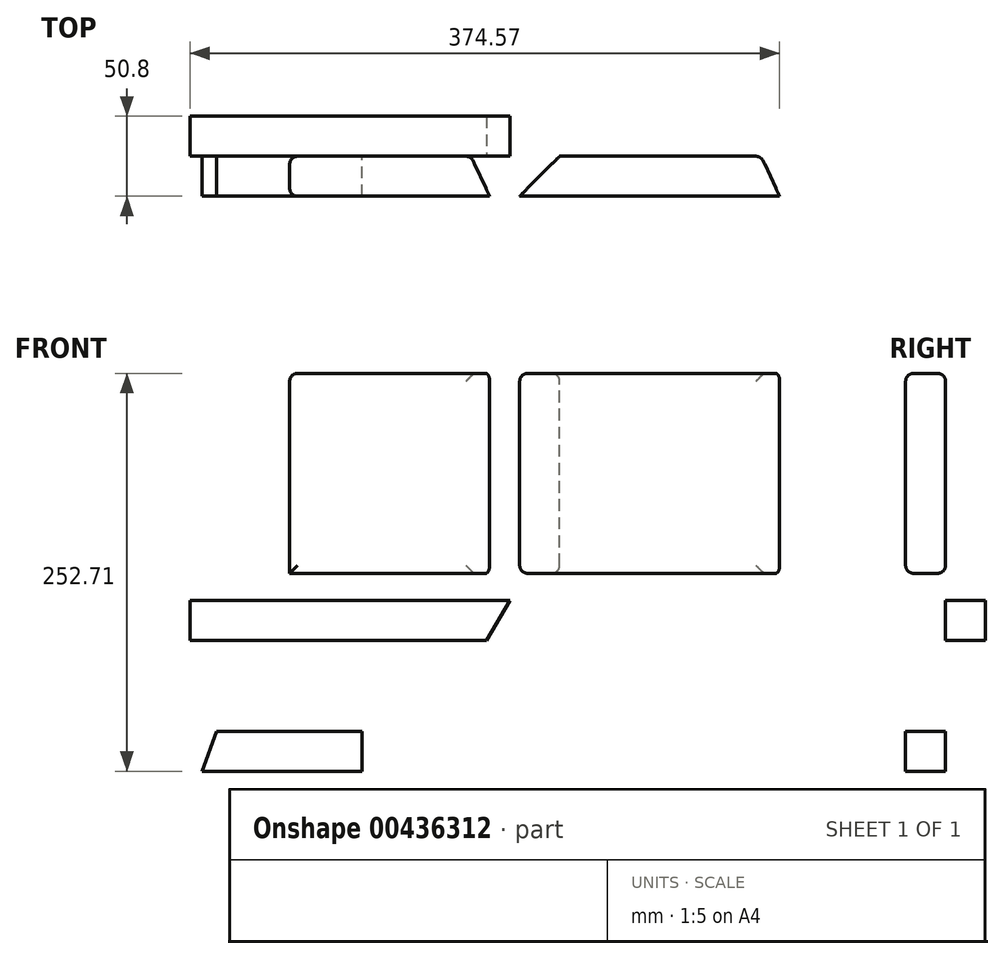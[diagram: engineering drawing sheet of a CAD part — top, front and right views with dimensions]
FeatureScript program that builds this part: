
annotation { "Feature Type Name" : "Feature", "Feature Type Description" : "" }
export const myFeature = defineFeature(function(context is Context, id is Id, definition is map)
    precondition{}
    {
        {
            var Q0;
            Q0=qCreatedBy(makeId("Front.planeOp"),FACE);
            var sketch = newSketch(context, id + "F0", { "sketchPlane" : qUnion([Q0])});
            skLineSegment(sketch, "E0", {"start": v(0, 0) * mm, "end": v(127, 0) * mm});
            skLineSegment(sketch, "E1", {"start": v(127, 0) * mm, "end": v(127, 127) * mm});
            skLineSegment(sketch, "E2", {"start": v(127, 127) * mm, "end": v(0, 127) * mm});
            skLineSegment(sketch, "E3", {"start": v(0, 127) * mm, "end": v(0, 0) * mm});
            skSolve(sketch);
        }
        {
            var Q0;
            Q0 = qSketchRegion(id + "F0", true);
            extrude(context, id + "F1", {"entities" : qUnion([Q0]), "depth" : 25.4 * mm});
        }
        {
            var Q0;
            Q0=makeQuery(id+"F1.opExtrude","CAP_EDGE",EDGE,{"disambiguationData":[OSD([sQuery(id+"F0.wireOp",EDGE,"E1")])],"isStart":true});
            chamfer(context, id + "F2", {"entities" : qUnion([Q0]), "chamferType" : ChamferType.OFFSET_ANGLE, "width" : 25.4 * mm, "oppositeDirection" : false, "angle" : 25 * degree, "tangentPropagation" : true});
        }
        {
            var Q0;
            Q0=qCreatedBy(makeId("Front.planeOp"),FACE);
            var sketch = newSketch(context, id + "F3", { "sketchPlane" : qUnion([Q0])});
            skLineSegment(sketch, "E4.bottom", {"start": v(146.1, 127) * mm, "end": v(311.2, 127) * mm});
            skLineSegment(sketch, "E4.top", {"start": v(146.1, 0) * mm, "end": v(311.2, 0) * mm});
            skLineSegment(sketch, "E4.left", {"start": v(146.1, 127) * mm, "end": v(146.1, 0) * mm});
            skLineSegment(sketch, "E4.right", {"start": v(311.2, 127) * mm, "end": v(311.2, 0) * mm});
            skSolve(sketch);
        }
        {
            var Q0;
            Q0 = qSketchRegion(id + "F3", true);
            extrude(context, id + "F4", {"entities" : qUnion([Q0]), "depth" : 25.4 * mm});
        }
        {
            var Q0;
            Q0=makeQuery(id+"F4.opExtrude","CAP_EDGE",EDGE,{"disambiguationData":[OSD([sQuery(id+"F3.wireOp",EDGE,"E4.right")])],"isStart":true});
            chamfer(context, id + "F5", {"entities" : qUnion([Q0]), "chamferType" : ChamferType.OFFSET_ANGLE, "width" : 25.4 * mm, "oppositeDirection" : true, "angle" : 25 * degree});
        }
        {
            var Q0;
            Q0=makeQuery(id+"F4.opExtrude","CAP_EDGE",EDGE,{"disambiguationData":[OSD([sQuery(id+"F3.wireOp",EDGE,"E4.left")])],"isStart":true});
            chamfer(context, id + "F6", {"entities" : qUnion([Q0]), "chamferType" : ChamferType.OFFSET_ANGLE, "width" : 25.4 * mm, "oppositeDirection" : false, "angle" : 45 * degree, "tangentPropagation" : true});
        }
        {
            var Q0;
            Q0=makeQuery(id+"F1.opExtrude","CAP_FACE",FACE,{"disambiguationData":[OSD([sQuery(id+"F0.wireOp",EDGE,"E0"),sQuery(id+"F0.wireOp",EDGE,"E1"),sQuery(id+"F0.wireOp",EDGE,"E2"),sQuery(id+"F0.wireOp",EDGE,"E3")])],"isStart":true});
            var sketch = newSketch(context, id + "F7", { "sketchPlane" : qUnion([Q0])});
            skLineSegment(sketch, "E5.bottom", {"start": v(63.38, -17.34) * mm, "end": v(-139.82, -17.34) * mm});
            skLineSegment(sketch, "E5.top", {"start": v(63.38, -42.74) * mm, "end": v(-139.82, -42.74) * mm});
            skLineSegment(sketch, "E5.left", {"start": v(63.38, -17.34) * mm, "end": v(63.38, -42.74) * mm});
            skLineSegment(sketch, "E5.right", {"start": v(-139.82, -17.34) * mm, "end": v(-139.82, -42.74) * mm});
            skSolve(sketch);
        }
        {
            var Q0;
            Q0 = qSketchRegion(id + "F7", true);
            extrude(context, id + "F8", {"entities" : qUnion([Q0]), "depth" : 25.4 * mm});
        }
        {
            var Q0;
            Q0=makeQuery(id+"F8.opExtrude","SWEPT_EDGE",EDGE,{"disambiguationData":[OSD([sQuery(id+"F7.wireOp",EDGE,"E5.top"),sQuery(id+"F7.wireOp",EDGE,"E5.right")])]});
            chamfer(context, id + "F9", {"entities" : qUnion([Q0]), "chamferType" : ChamferType.OFFSET_ANGLE, "width" : 25.4 * mm, "oppositeDirection" : true, "angle" : 30 * degree, "tangentPropagation" : true});
        }
        {
            var Q0;
            Q0=makeQuery(id+"F1.opExtrude","CAP_EDGE",EDGE,{"disambiguationData":[OSD([sQuery(id+"F0.wireOp",EDGE,"E2")])],"isStart":false});
            var Q1;
            Q1=makeQuery(id+"F1.opExtrude","CAP_EDGE",EDGE,{"disambiguationData":[OSD([sQuery(id+"F0.wireOp",EDGE,"E2")])],"isStart":true});
            var Q2;
            Q2=makeQuery(id+"F1.opExtrude","CAP_EDGE",EDGE,{"disambiguationData":[OSD([sQuery(id+"F0.wireOp",EDGE,"E3")])],"isStart":false});
            var Q3;
            Q3=makeQuery(id+"F1.opExtrude","SWEPT_EDGE",EDGE,{"disambiguationData":[OSD([sQuery(id+"F0.wireOp",EDGE,"E2"),sQuery(id+"F0.wireOp",EDGE,"E3")])]});
            var Q4;
            Q4=makeQuery(id+"F1.opExtrude","CAP_EDGE",EDGE,{"disambiguationData":[OSD([sQuery(id+"F0.wireOp",EDGE,"E0")])],"isStart":false});
            var Q5;
            Q5=makeQuery(id+"F4.opExtrude","CAP_EDGE",EDGE,{"disambiguationData":[OSD([sQuery(id+"F3.wireOp",EDGE,"E4.top")])],"isStart":true});
            var Q6;
            {var subQ0=sQuery(id+"F3.wireOp",EDGE,"E4.right");Q6=makeQuery(id+"F5.opChamfer","BLEND_EDGE",EDGE,{"blendedFrom":[makeQuery(id+"F4.opExtrude","CAP_EDGE",EDGE,{"disambiguationData":[OSD([subQ0])],"isStart":true}),makeQuery(id+"F4.opExtrude","CAP_FACE",FACE,{"disambiguationData":[OSD([sQuery(id+"F3.wireOp",EDGE,"E4.bottom"),sQuery(id+"F3.wireOp",EDGE,"E4.top"),sQuery(id+"F3.wireOp",EDGE,"E4.left"),subQ0])],"isStart":true})],"blendedInto":[makeQuery(id+"F4.opExtrude","CAP_FACE",FACE,{"disambiguationData":[OSD([sQuery(id+"F3.wireOp",EDGE,"E4.bottom"),sQuery(id+"F3.wireOp",EDGE,"E4.top"),sQuery(id+"F3.wireOp",EDGE,"E4.left"),subQ0])],"isStart":true})]});}
            var Q7;
            Q7=makeQuery(id+"F4.opExtrude","CAP_EDGE",EDGE,{"disambiguationData":[OSD([sQuery(id+"F3.wireOp",EDGE,"E4.bottom")])],"isStart":true});
            var Q8;
            Q8=makeQuery(id+"F4.opExtrude","CAP_EDGE",EDGE,{"disambiguationData":[OSD([sQuery(id+"F3.wireOp",EDGE,"E4.bottom")])],"isStart":false});
            var Q9;
            {var subQ0=sQuery(id+"F0.wireOp",EDGE,"E1");Q9=makeQuery(id+"F2.opChamfer","BLEND_EDGE",EDGE,{"blendedFrom":[makeQuery(id+"F1.opExtrude","CAP_EDGE",EDGE,{"disambiguationData":[OSD([subQ0])],"isStart":true}),makeQuery(id+"F1.opExtrude","CAP_FACE",FACE,{"disambiguationData":[OSD([sQuery(id+"F0.wireOp",EDGE,"E0"),subQ0,sQuery(id+"F0.wireOp",EDGE,"E2"),sQuery(id+"F0.wireOp",EDGE,"E3")])],"isStart":true})],"blendedInto":[makeQuery(id+"F1.opExtrude","CAP_FACE",FACE,{"disambiguationData":[OSD([sQuery(id+"F0.wireOp",EDGE,"E0"),subQ0,sQuery(id+"F0.wireOp",EDGE,"E2"),sQuery(id+"F0.wireOp",EDGE,"E3")])],"isStart":true})]});}
            var Q10;
            Q10=makeQuery(id+"F1.opExtrude","CAP_EDGE",EDGE,{"disambiguationData":[OSD([sQuery(id+"F0.wireOp",EDGE,"E0")])],"isStart":true});
            var Q11;
            Q11=makeQuery(id+"F1.opExtrude","CAP_EDGE",EDGE,{"disambiguationData":[OSD([sQuery(id+"F0.wireOp",EDGE,"E3")])],"isStart":true});
            var Q12;
            Q12=makeQuery(id+"F4.opExtrude","CAP_EDGE",EDGE,{"disambiguationData":[OSD([sQuery(id+"F3.wireOp",EDGE,"E4.top")])],"isStart":false});
            fillet(context, id + "F10", {"entities" : qUnion([Q0, Q1, Q2, Q3, Q4, Q5, Q6, Q7, Q8, Q9, Q10, Q11, Q12]), "radius" : 5.08 * mm, "tangentPropagation" : true, "allowEdgeOverflow" : false});
        }
        {
            var Q0;
            Q0=qCreatedBy(makeId("Front.planeOp"),FACE);
            var sketch = newSketch(context, id + "F11", { "sketchPlane" : qUnion([Q0])});
            skLineSegment(sketch, "E6.bottom", {"start": v(-55.54, -100.3) * mm, "end": v(46.06, -100.3) * mm});
            skLineSegment(sketch, "E6.top", {"start": v(-55.54, -125.7) * mm, "end": v(46.06, -125.7) * mm});
            skLineSegment(sketch, "E6.left", {"start": v(-55.54, -100.3) * mm, "end": v(-55.54, -125.7) * mm});
            skLineSegment(sketch, "E6.right", {"start": v(46.06, -100.3) * mm, "end": v(46.06, -125.7) * mm});
            skSolve(sketch);
        }
        {
            var Q0;
            Q0 = qSketchRegion(id + "F11", true);
            extrude(context, id + "F12", {"entities" : qUnion([Q0]), "depth" : 25.4 * mm});
        }
        {
            var Q0;
            Q0=makeQuery(id+"F12.opExtrude","SWEPT_EDGE",EDGE,{"disambiguationData":[OSD([sQuery(id+"F11.wireOp",EDGE,"E6.bottom"),sQuery(id+"F11.wireOp",EDGE,"E6.left")])]});
            chamfer(context, id + "F13", {"entities" : qUnion([Q0]), "chamferType" : ChamferType.OFFSET_ANGLE, "width" : 25.4 * mm, "oppositeDirection" : false, "angle" : 20 * degree, "tangentPropagation" : true});
        }
    });
